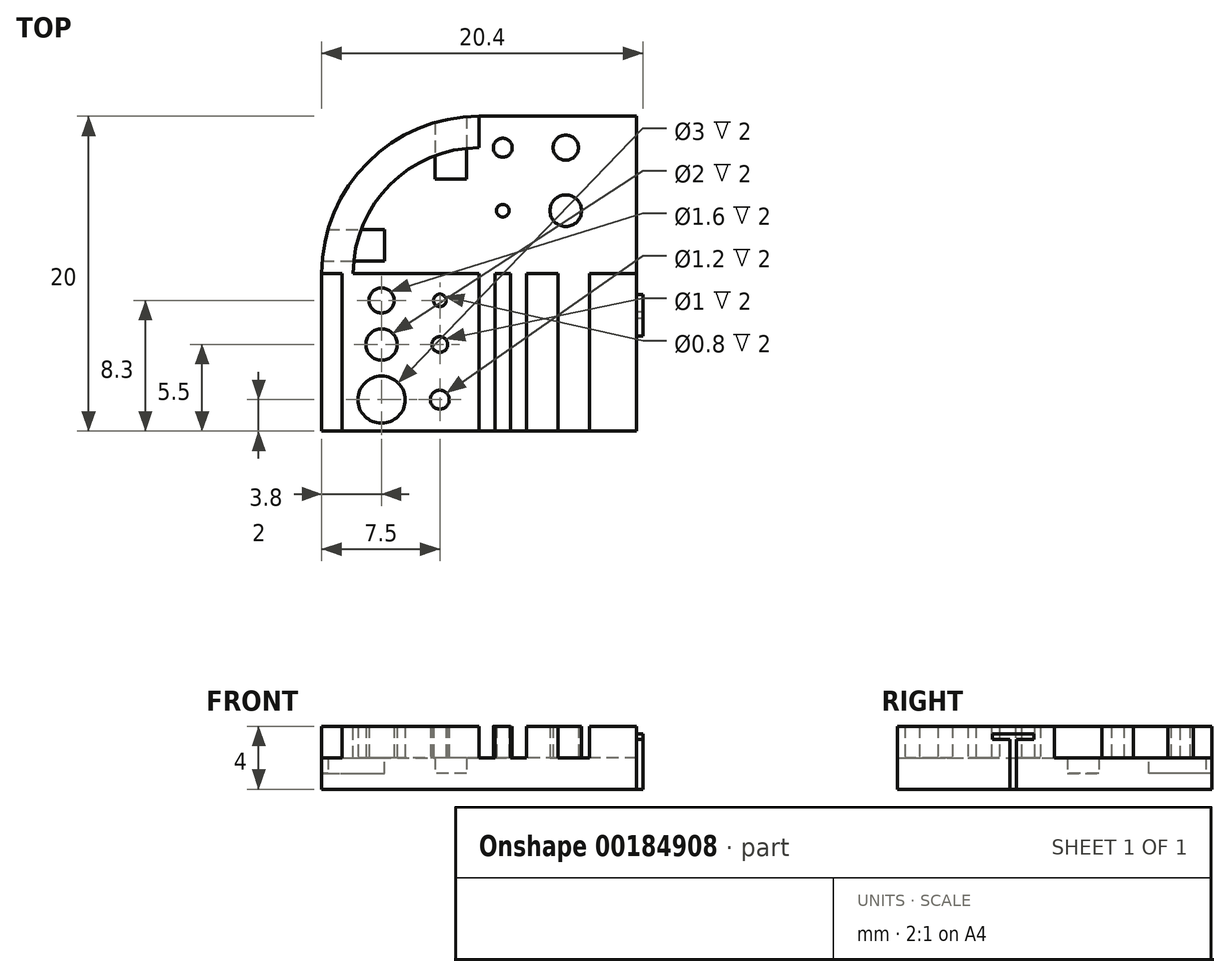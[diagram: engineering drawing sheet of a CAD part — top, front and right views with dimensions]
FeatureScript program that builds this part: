
annotation { "Feature Type Name" : "Feature", "Feature Type Description" : "" }
export const myFeature = defineFeature(function(context is Context, id is Id, definition is map)
    precondition{}
    {
        {
            var Q0;
            Q0=qCreatedBy(makeId("Top.planeOp"),FACE);
            var sketch = newSketch(context, id + "F0", { "sketchPlane" : qUnion([Q0])});
            skLineSegment(sketch, "E0.bottom", {"start": v(10, -10) * mm, "end": v(-10, -10) * mm});
            skLineSegment(sketch, "E0.top", {"start": v(10, 10) * mm, "end": v(0, 10) * mm});
            skLineSegment(sketch, "E0.left", {"start": v(10, -10) * mm, "end": v(10, 10) * mm});
            skLineSegment(sketch, "E0.right", {"start": v(-10, -10) * mm, "end": v(-10, 0) * mm});
            skPoint(sketch, "E0.middle", {"position": v(0, 0) * mm});
            skPoint(sketch, "E1.visualSharp", {"position": v(-10, 10) * mm});
            skArc(sketch, "E1.filletArc", {"start": v(0, 10) * mm, "mid": v(-7.07, 7.07) * mm, "end": v(-10, 0) * mm});
            skSolve(sketch);
        }
        {
            var Q0;
            Q0=makeQuery(id+"F0.imprint","IMPRINT",FACE,{"disambiguationData":[TD([[makeQuery(id+"F0.imprint","IMPRINT",EDGE,{"derivedFrom":sQuery(id+"F0.wireOp",EDGE,"E0.bottom")}),-1.0]])]});
            extrude(context, id + "F1", {"entities" : qUnion([Q0]), "depth" : 2 * mm});
        }
        {
            var Q0;
            Q0=makeQuery(id+"F1.opExtrude","CAP_FACE",FACE,{"disambiguationData":[OSD([sQuery(id+"F0.wireOp",EDGE,"E0.bottom"),sQuery(id+"F0.wireOp",EDGE,"E0.top"),sQuery(id+"F0.wireOp",EDGE,"E0.left"),sQuery(id+"F0.wireOp",EDGE,"E0.right"),sQuery(id+"F0.wireOp",EDGE,"E1.filletArc")])],"isStart":false});
            var sketch = newSketch(context, id + "F2", { "sketchPlane" : qUnion([Q0])});
            skLineSegment(sketch, "E2.bottom", {"start": v(10, -10) * mm, "end": v(7, -10) * mm});
            skLineSegment(sketch, "E2.top", {"start": v(10, 0) * mm, "end": v(7, 0) * mm});
            skLineSegment(sketch, "E2.left", {"start": v(10, -10) * mm, "end": v(10, 0) * mm});
            skLineSegment(sketch, "E2.right", {"start": v(7, -10) * mm, "end": v(7, 0) * mm});
            skLineSegment(sketch, "E3.bottom", {"start": v(5, -10) * mm, "end": v(3, -10) * mm});
            skLineSegment(sketch, "E3.top", {"start": v(5, 0) * mm, "end": v(3, 0) * mm});
            skLineSegment(sketch, "E3.left", {"start": v(5, -10) * mm, "end": v(5, 0) * mm});
            skLineSegment(sketch, "E3.right", {"start": v(3, -10) * mm, "end": v(3, 0) * mm});
            skLineSegment(sketch, "E4.bottom", {"start": v(2, -10) * mm, "end": v(1, -10) * mm});
            skLineSegment(sketch, "E4.top", {"start": v(2, 0) * mm, "end": v(1, 0) * mm});
            skLineSegment(sketch, "E4.left", {"start": v(2, -10) * mm, "end": v(2, 0) * mm});
            skLineSegment(sketch, "E4.right", {"start": v(1, -10) * mm, "end": v(1, 0) * mm});
            skLineSegment(sketch, "E5.bottom", {"start": v(0, -10) * mm, "end": v(-8.7, -10) * mm});
            skLineSegment(sketch, "E5.top", {"start": v(0, 0) * mm, "end": v(-8.7, 0) * mm});
            skLineSegment(sketch, "E5.left", {"start": v(0, -10) * mm, "end": v(0, 0) * mm});
            skLineSegment(sketch, "E5.right", {"start": v(-8.7, -10) * mm, "end": v(-8.7, 0) * mm});
            skCircle(sketch, "E6", {"center": v(-6.2, -8) * mm, "radius": 1.5 * mm});
            skCircle(sketch, "E7", {"center": v(-6.2, -4.5) * mm, "radius": 1 * mm});
            skPoint(sketch, "E7.centerSnap0", {"position": v(-4.35, -10) * mm});
            skCircle(sketch, "E8", {"center": v(-6.2, -1.7) * mm, "radius": 0.8 * mm});
            skCircle(sketch, "E9", {"center": v(-2.5, -8) * mm, "radius": 0.6 * mm});
            skLineSegment(sketch, "E10", {"start": v(-6.2, -10) * mm, "end": v(-6.2, 0) * mm, "construction": true});
            skLineSegment(sketch, "E11", {"start": v(-2.5, -10) * mm, "end": v(-2.5, 0) * mm, "construction": true});
            skCircle(sketch, "E12", {"center": v(-2.5, -4.5) * mm, "radius": 0.5 * mm});
            skCircle(sketch, "E13", {"center": v(-2.5, -1.7) * mm, "radius": 0.4 * mm});
            skCircle(sketch, "E14", {"center": v(1.5, 4) * mm, "radius": 0.4 * mm});
            skCircle(sketch, "E15", {"center": v(1.5, 8) * mm, "radius": 0.6 * mm});
            skCircle(sketch, "E16", {"center": v(5.5, 8) * mm, "radius": 0.8 * mm});
            skCircle(sketch, "E17", {"center": v(5.5, 4) * mm, "radius": 1 * mm});
            skLineSegment(sketch, "E18", {"start": v(1.5, 0) * mm, "end": v(1.5, 10) * mm, "construction": true});
            skLineSegment(sketch, "E19", {"start": v(5.5, 0) * mm, "end": v(5.5, 10) * mm, "construction": true});
            skLineSegment(sketch, "E20", {"start": v(10, 8) * mm, "end": v(0, 8) * mm, "construction": true});
            skLineSegment(sketch, "E21", {"start": v(10, 4) * mm, "end": v(0, 4) * mm, "construction": true});
            skSolve(sketch);
        }
        {
            var Q0;
            Q0=makeQuery(id+"F2.imprint","IMPRINT",FACE,{"disambiguationData":[TD([[makeQuery(id+"F2.imprint","IMPRINT",EDGE,{"derivedFrom":sQuery(id+"F2.wireOp",EDGE,"E5.bottom")}),-1.0]])]});
            var Q1;
            Q1=makeQuery(id+"F2.imprint","IMPRINT",FACE,{"disambiguationData":[TD([[makeQuery(id+"F2.imprint","IMPRINT",EDGE,{"derivedFrom":sQuery(id+"F2.wireOp",EDGE,"E2.bottom")}),-1.0]])]});
            var Q2;
            Q2=makeQuery(id+"F2.imprint","IMPRINT",FACE,{"disambiguationData":[TD([[makeQuery(id+"F2.imprint","IMPRINT",EDGE,{"derivedFrom":sQuery(id+"F2.wireOp",EDGE,"E3.bottom")}),-1.0]])]});
            var Q3;
            Q3=makeQuery(id+"F2.imprint","IMPRINT",FACE,{"disambiguationData":[TD([[makeQuery(id+"F2.imprint","IMPRINT",EDGE,{"derivedFrom":sQuery(id+"F2.wireOp",EDGE,"E4.bottom")}),-1.0]])]});
            var Q4;
            Q4=makeQuery(id+"F2.imprint","IMPRINT",FACE,{"disambiguationData":[TD([[makeQuery(id+"F2.imprint","IMPRINT",EDGE,{"derivedFrom":sQuery(id+"F2.wireOp",EDGE,"E14")}),1.0]])]});
            var Q5;
            Q5=makeQuery(id+"F2.imprint","IMPRINT",FACE,{"disambiguationData":[TD([[makeQuery(id+"F2.imprint","IMPRINT",EDGE,{"derivedFrom":sQuery(id+"F2.wireOp",EDGE,"E17")}),1.0]])]});
            var Q6;
            Q6=makeQuery(id+"F2.imprint","IMPRINT",FACE,{"disambiguationData":[TD([[makeQuery(id+"F2.imprint","IMPRINT",EDGE,{"derivedFrom":sQuery(id+"F2.wireOp",EDGE,"E16")}),1.0]])]});
            var Q7;
            Q7=makeQuery(id+"F2.imprint","IMPRINT",FACE,{"disambiguationData":[TD([[makeQuery(id+"F2.imprint","IMPRINT",EDGE,{"derivedFrom":sQuery(id+"F2.wireOp",EDGE,"E15")}),1.0]])]});
            extrude(context, id + "F3", {"entities" : qUnion([Q0, Q1, Q2, Q3, Q4, Q5, Q6, Q7]), "operationType" : NewBodyOperationType.ADD, "depth" : 2 * mm});
        }
        {
            var Q0;
            Q0=qCreatedBy(makeId("Right.planeOp"),FACE);
            var sketch = newSketch(context, id + "F4", { "sketchPlane" : qUnion([Q0])});
            skLineSegment(sketch, "E22.bottom", {"start": v(10, 2) * mm, "end": v(8, 2) * mm});
            skLineSegment(sketch, "E22.top", {"start": v(10, 4) * mm, "end": v(8, 4) * mm});
            skLineSegment(sketch, "E22.left", {"start": v(10, 2) * mm, "end": v(10, 4) * mm});
            skLineSegment(sketch, "E22.right", {"start": v(8, 2) * mm, "end": v(8, 4) * mm});
            skLineSegment(sketch, "E23", {"start": v(0, 0) * mm, "end": v(0, 12.9) * mm, "construction": true});
            skSolve(sketch);
        }
        {
            var Q0;
            Q0=makeQuery(id+"F4.imprint","IMPRINT",FACE,{"disambiguationData":[TD([[makeQuery(id+"F4.imprint","IMPRINT",EDGE,{"derivedFrom":sQuery(id+"F4.wireOp",EDGE,"E22.bottom")}),-1.0]])]});
            var Q1;
            Q1=sQuery(id+"F4.wireOp",EDGE,"E23");
            revolve(context, id + "F5", {"operationType" : NewBodyOperationType.ADD, "entities" : qUnion([Q0]), "axis" : qUnion([Q1]), "revolveType" : RevolveType.ONE_DIRECTION, "angle" : 90 * degree});
        }
        {
            var Q0;
            {var subQ0=sQuery(id+"F0.wireOp",EDGE,"E0.left");var subQ1=sQuery(id+"F0.wireOp",EDGE,"E0.right");var subQ2=sQuery(id+"F0.wireOp",EDGE,"E0.top");var subQ3=sQuery(id+"F0.wireOp",EDGE,"E0.bottom");var subQ4=sQuery(id+"F0.wireOp",EDGE,"E1.filletArc");Q0=makeQuery(id+"F3.boolean.opBoolean","SPLIT",FACE,{"disambiguationData":[TD([makeQuery(id+"F1.opExtrude","SWEPT_FACE",FACE,{"disambiguationData":[OSD([subQ3])]})])],"derivedFrom":makeQuery(id+"F1.opExtrude","CAP_FACE",FACE,{"disambiguationData":[OSD([subQ3,subQ2,subQ0,subQ1,subQ4])],"isStart":false})});}
            var sketch = newSketch(context, id + "F6", { "sketchPlane" : qUnion([Q0])});
            skLineSegment(sketch, "E24.bottom", {"start": v(-0.8, 10) * mm, "end": v(-2.8, 10) * mm});
            skLineSegment(sketch, "E24.top", {"start": v(-0.8, 6) * mm, "end": v(-2.8, 6) * mm});
            skLineSegment(sketch, "E24.left", {"start": v(-0.8, 10) * mm, "end": v(-0.8, 6) * mm});
            skLineSegment(sketch, "E24.right", {"start": v(-2.8, 10) * mm, "end": v(-2.8, 6) * mm});
            skLineSegment(sketch, "E25.bottom", {"start": v(-10, 0.8) * mm, "end": v(-6, 0.8) * mm});
            skLineSegment(sketch, "E25.top", {"start": v(-10, 2.8) * mm, "end": v(-6, 2.8) * mm});
            skLineSegment(sketch, "E25.left", {"start": v(-10, 0.8) * mm, "end": v(-10, 2.8) * mm});
            skLineSegment(sketch, "E25.right", {"start": v(-6, 0.8) * mm, "end": v(-6, 2.8) * mm});
            skSolve(sketch);
        }
        {
            var Q0;
            {var subQ0=sQuery(id+"F6.wireOp",EDGE,"E25.left");Q0=makeQuery(id+"F6.imprint","IMPRINT",FACE,{"disambiguationData":[TD([[makeQuery(id+"F6.imprint","IMPRINT",EDGE,{"derivedFrom":subQ0}),-1.0]])]});}
            var Q1;
            {var subQ0=sQuery(id+"F6.wireOp",EDGE,"E24.bottom");Q1=makeQuery(id+"F6.imprint","IMPRINT",FACE,{"disambiguationData":[TD([[makeQuery(id+"F6.imprint","IMPRINT",EDGE,{"derivedFrom":subQ0}),1.0]])]});}
            var Q2;
            {var subQ0=sQuery(id+"F6.wireOp",EDGE,"E25.right");Q2=makeQuery(id+"F6.imprint","IMPRINT",FACE,{"disambiguationData":[TD([[makeQuery(id+"F6.imprint","IMPRINT",EDGE,{"derivedFrom":subQ0}),1.0]])]});}
            var Q3;
            {var subQ0=sQuery(id+"F6.wireOp",EDGE,"E24.top");Q3=makeQuery(id+"F6.imprint","IMPRINT",FACE,{"disambiguationData":[TD([[makeQuery(id+"F6.imprint","IMPRINT",EDGE,{"derivedFrom":subQ0}),-1.0]])]});}
            extrude(context, id + "F7", {"entities" : qUnion([Q0, Q1, Q2, Q3]), "operationType" : NewBodyOperationType.REMOVE, "oppositeDirection" : true, "depth" : 1 * mm});
        }
        {
            var Q0;
            Q0=makeQuery(id+"F3.boolean.opBoolean","MERGE",FACE,{"derivedFrom":[makeQuery(id+"F1.opExtrude","SWEPT_FACE",FACE,{"disambiguationData":[OSD([sQuery(id+"F0.wireOp",EDGE,"E0.left")])]}),makeQuery(id+"F3.opExtrude","SWEPT_FACE",FACE,{"disambiguationData":[OSD([sQuery(id+"F2.wireOp",EDGE,"E2.left")])]})]});
            var sketch = newSketch(context, id + "F8", { "sketchPlane" : qUnion([Q0])});
            skText(sketch, "E26", { "text": "T", "fontName": "OpenSans-Regular.ttf"});
            const initialGuessF8  = {"E26": [-0.004, 0, 1, 0, 0.00355]};
            skSetInitialGuess(sketch, initialGuessF8);
            skSolve(sketch);
        }
        {
            var Q0;
            Q0=makeQuery(id+"F8.imprint","IMPRINT",FACE,{"disambiguationData":[TD([[makeQuery(id+"F8.imprint","IMPRINT",EDGE,{"derivedFrom":sQuery(id+"F8.wireOp",EDGE,"E26.sketch_text.stroke-0")}),1.0]])]});
            extrude(context, id + "F9", {"entities" : qUnion([Q0]), "operationType" : NewBodyOperationType.ADD, "depth" : 0.4 * mm});
        }
    });
